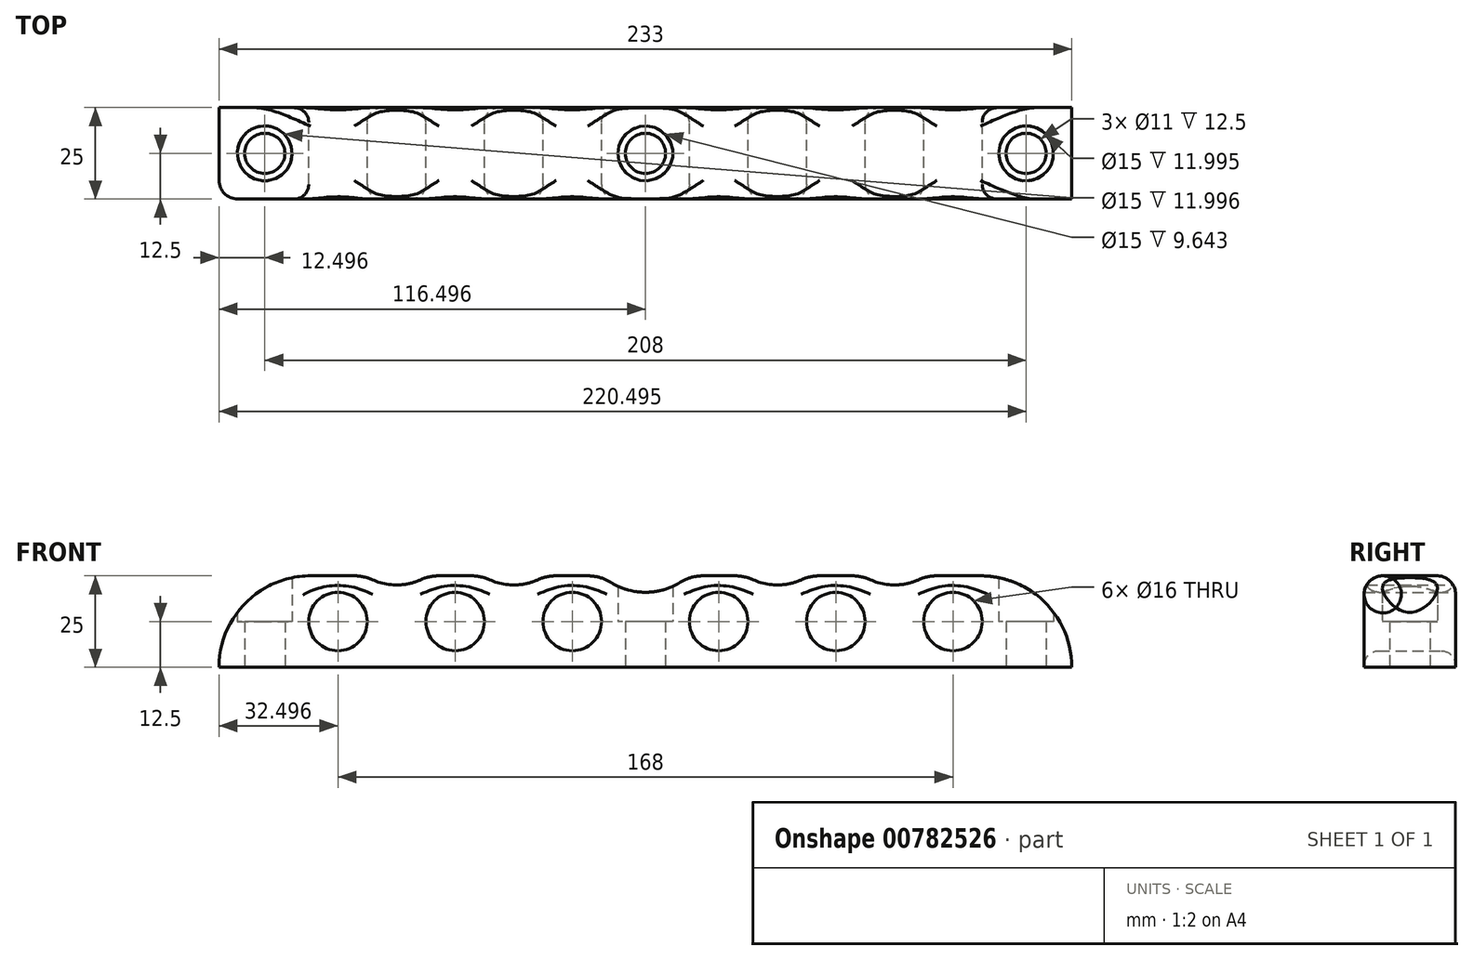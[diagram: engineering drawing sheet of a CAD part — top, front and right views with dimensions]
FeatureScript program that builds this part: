
annotation { "Feature Type Name" : "Feature", "Feature Type Description" : "" }
export const myFeature = defineFeature(function(context is Context, id is Id, definition is map)
    precondition{}
    {
        {
            var Q0;
            Q0=qCreatedBy(makeId("Front.planeOp"),FACE);
            var sketch = newSketch(context, id + "F0", { "sketchPlane" : qUnion([Q0])});
            skLineSegment(sketch, "E0", {"start": v(-90.93, 0) * mm, "end": v(142.07, 0) * mm});
            skArc(sketch, "E1", {"start": v(-90.93, 0) * mm, "mid": v(-77.77, 22.02) * mm, "end": v(-52.14, 20.85) * mm});
            skArc(sketch, "E2", {"start": v(142.07, 0) * mm, "mid": v(127.68, 22.63) * mm, "end": v(101.09, 19.23) * mm});
            skCircle(sketch, "E3", {"center": v(-58.43, 12.5) * mm, "radius": 8 * mm});
            skCircle(sketch, "E4", {"center": v(-26.43, 12.5) * mm, "radius": 8 * mm});
            skCircle(sketch, "E5", {"center": v(5.57, 12.5) * mm, "radius": 8 * mm});
            skCircle(sketch, "E6", {"center": v(45.57, 12.5) * mm, "radius": 8 * mm});
            skCircle(sketch, "E7", {"center": v(77.57, 12.5) * mm, "radius": 8 * mm});
            skCircle(sketch, "E8", {"center": v(109.57, 12.5) * mm, "radius": 8 * mm});
            skLineSegment(sketch, "E9", {"start": v(-65.93, 25) * mm, "end": v(117.07, 25) * mm});
            skCircle(sketch, "E10", {"center": v(-42.43, 38.5) * mm, "radius": 16 * mm});
            skCircle(sketch, "E11", {"center": v(-10.43, 38.5) * mm, "radius": 16 * mm});
            skCircle(sketch, "E12", {"center": v(25.57, 38.5) * mm, "radius": 18 * mm});
            skCircle(sketch, "E13", {"center": v(61.57, 38.5) * mm, "radius": 16 * mm});
            skCircle(sketch, "E14", {"center": v(93.57, 38.5) * mm, "radius": 16 * mm});
            skSolve(sketch);
        }
        {
            var Q0;
            {var subQ6=sQuery(id+"F0.wireOp",EDGE,"E0");Q0=makeQuery(id+"F0.imprint","IMPRINT",FACE,{"disambiguationData":[TD([[makeQuery(id+"F0.imprint","IMPRINT",EDGE,{"derivedFrom":subQ6}),1.0]])]});}
            extrude(context, id + "F1", {"entities" : qUnion([Q0]), "depth" : 25 * mm, "offsetDistance" : 25.4 * mm});
        }
        {
            var Q0;
            Q0=makeQuery(id+"F1.opExtrude","CAP_EDGE",EDGE,{"disambiguationData":[OSD([sQuery(id+"F0.wireOp",EDGE,"E3")])],"isStart":false});
            var Q1;
            Q1=makeQuery(id+"F1.opExtrude","CAP_EDGE",EDGE,{"disambiguationData":[OSD([sQuery(id+"F0.wireOp",EDGE,"E4")])],"isStart":false});
            var Q2;
            Q2=makeQuery(id+"F1.opExtrude","CAP_EDGE",EDGE,{"disambiguationData":[OSD([sQuery(id+"F0.wireOp",EDGE,"E5")])],"isStart":false});
            var Q3;
            Q3=makeQuery(id+"F1.opExtrude","CAP_EDGE",EDGE,{"disambiguationData":[OSD([sQuery(id+"F0.wireOp",EDGE,"E6")])],"isStart":false});
            var Q4;
            Q4=makeQuery(id+"F1.opExtrude","CAP_EDGE",EDGE,{"disambiguationData":[OSD([sQuery(id+"F0.wireOp",EDGE,"E7")])],"isStart":true});
            var Q5;
            Q5=makeQuery(id+"F1.opExtrude","CAP_EDGE",EDGE,{"disambiguationData":[OSD([sQuery(id+"F0.wireOp",EDGE,"E7")])],"isStart":false});
            var Q6;
            Q6=makeQuery(id+"F1.opExtrude","CAP_EDGE",EDGE,{"disambiguationData":[OSD([sQuery(id+"F0.wireOp",EDGE,"E8")])],"isStart":false});
            var Q7;
            Q7=makeQuery(id+"F1.opExtrude","CAP_EDGE",EDGE,{"disambiguationData":[OSD([sQuery(id+"F0.wireOp",EDGE,"E8")])],"isStart":true});
            var Q8;
            Q8=makeQuery(id+"F1.opExtrude","CAP_EDGE",EDGE,{"disambiguationData":[OSD([sQuery(id+"F0.wireOp",EDGE,"E6")])],"isStart":true});
            var Q9;
            Q9=makeQuery(id+"F1.opExtrude","CAP_EDGE",EDGE,{"disambiguationData":[OSD([sQuery(id+"F0.wireOp",EDGE,"E5")])],"isStart":true});
            var Q10;
            Q10=makeQuery(id+"F1.opExtrude","CAP_EDGE",EDGE,{"disambiguationData":[OSD([sQuery(id+"F0.wireOp",EDGE,"E4")])],"isStart":true});
            var Q11;
            Q11=makeQuery(id+"F1.opExtrude","CAP_EDGE",EDGE,{"disambiguationData":[OSD([sQuery(id+"F0.wireOp",EDGE,"E3")])],"isStart":true});
            fillet(context, id + "F2", {"entities" : qUnion([Q0, Q1, Q2, Q3, Q4, Q5, Q6, Q7, Q8, Q9, Q10, Q11]), "radius" : 4 * mm, "tangentPropagation" : true, "allowEdgeOverflow" : false});
        }
        {
            var Q0;
            Q0=qCreatedBy(makeId("Top.planeOp"),FACE);
            var sketch = newSketch(context, id + "F3", { "sketchPlane" : qUnion([Q0])});
            skCircle(sketch, "E15", {"center": v(-78.43, -12.5) * mm, "radius": 7.5 * mm});
            skCircle(sketch, "E16", {"center": v(129.57, -12.5) * mm, "radius": 7.5 * mm});
            skCircle(sketch, "E17", {"center": v(-78.43, -12.5) * mm, "radius": 5.5 * mm});
            skCircle(sketch, "E18", {"center": v(129.57, -12.5) * mm, "radius": 5.5 * mm});
            skCircle(sketch, "E19", {"center": v(25.57, -12.5) * mm, "radius": 7.5 * mm});
            skCircle(sketch, "E20", {"center": v(25.57, -12.5) * mm, "radius": 5.5 * mm});
            skSolve(sketch);
        }
        {
            var Q0;
            Q0=makeQuery(id+"F3.imprint","IMPRINT",FACE,{"disambiguationData":[TD([[makeQuery(id+"F3.imprint","IMPRINT",EDGE,{"derivedFrom":sQuery(id+"F3.wireOp",EDGE,"E17")}),1.0]])]});
            var Q1;
            Q1=makeQuery(id+"F3.imprint","IMPRINT",FACE,{"disambiguationData":[TD([[makeQuery(id+"F3.imprint","IMPRINT",EDGE,{"derivedFrom":sQuery(id+"F3.wireOp",EDGE,"E18")}),1.0]])]});
            extrude(context, id + "F4", {"entities" : qUnion([Q0, Q1]), "operationType" : NewBodyOperationType.REMOVE, "depth" : 25.4 * mm, "offsetDistance" : 25.4 * mm});
        }
        {
            var Q0;
            Q0=makeQuery(id+"F3.imprint","IMPRINT",FACE,{"disambiguationData":[TD([[makeQuery(id+"F3.imprint","IMPRINT",EDGE,{"derivedFrom":sQuery(id+"F3.wireOp",EDGE,"E15")}),1.0]])]});
            var Q1;
            Q1=makeQuery(id+"F3.imprint","IMPRINT",FACE,{"disambiguationData":[TD([[makeQuery(id+"F3.imprint","IMPRINT",EDGE,{"derivedFrom":sQuery(id+"F3.wireOp",EDGE,"E16")}),1.0]])]});
            extrude(context, id + "F5", {"entities" : qUnion([Q0, Q1]), "operationType" : NewBodyOperationType.REMOVE, "depth" : 25.4 * mm, "offsetDistance" : 25.4 * mm});
        }
        {
            var Q0;
            Q0=makeQuery(id+"F3.imprint","IMPRINT",FACE,{"disambiguationData":[TD([[makeQuery(id+"F3.imprint","IMPRINT",EDGE,{"derivedFrom":sQuery(id+"F3.wireOp",EDGE,"E16")}),1.0]])]});
            var Q1;
            Q1=makeQuery(id+"F3.imprint","IMPRINT",FACE,{"disambiguationData":[TD([[makeQuery(id+"F3.imprint","IMPRINT",EDGE,{"derivedFrom":sQuery(id+"F3.wireOp",EDGE,"E15")}),1.0]])]});
            extrude(context, id + "F6", {"entities" : qUnion([Q0, Q1]), "operationType" : NewBodyOperationType.ADD, "depth" : 12.5 * mm, "offsetDistance" : 25.4 * mm});
        }
        {
            var Q0;
            {var subQ0=sQuery(id+"F0.wireOp",EDGE,"E9");Q0=makeQuery(id+"F1.opExtrude","CAP_EDGE",EDGE,{"disambiguationData":[OSD([subQ0]),TDD([makeQuery(id+"F0.imprint","IMPRINT",EDGE,{"disambiguationData":[TD([[makeQuery(id+"F0.imprint","INTERSECT",VERTEX,{"derivedFrom":[sQuery(id+"F0.wireOp",EDGE,"E1"),subQ0]}),-1.0]])],"derivedFrom":subQ0})])],"isStart":false});}
            var Q1;
            {var subQ0=sQuery(id+"F0.wireOp",EDGE,"E9");Q1=makeQuery(id+"F1.opExtrude","CAP_EDGE",EDGE,{"disambiguationData":[OSD([subQ0]),TDD([makeQuery(id+"F0.imprint","IMPRINT",EDGE,{"disambiguationData":[TD([[makeQuery(id+"F0.imprint","INTERSECT",VERTEX,{"disambiguationData":[OD(1.0)],"derivedFrom":[subQ0,sQuery(id+"F0.wireOp",EDGE,"E13")]}),-1.0]])],"derivedFrom":subQ0})])],"isStart":true});}
            fillet(context, id + "F7", {"entities" : qUnion([Q0, Q1]), "radius" : 5.08 * mm, "tangentPropagation" : true, "allowEdgeOverflow" : false});
        }
        {
            var Q0;
            {var subQ0=sQuery(id+"F0.wireOp",EDGE,"E10");var subQ1=sQuery(id+"F0.wireOp",EDGE,"E9");Q0=makeQuery(id+"F1.opExtrude","SWEPT_EDGE",EDGE,{"disambiguationData":[OSD([subQ1,subQ0]),TDD([makeQuery(id+"F0.imprint","INTERSECT",VERTEX,{"disambiguationData":[OD(0.0)],"derivedFrom":[subQ1,subQ0]})])]});}
            var Q1;
            {var subQ0=sQuery(id+"F0.wireOp",EDGE,"E10");var subQ1=sQuery(id+"F0.wireOp",EDGE,"E9");Q1=makeQuery(id+"F1.opExtrude","SWEPT_EDGE",EDGE,{"disambiguationData":[OSD([subQ1,subQ0]),TDD([makeQuery(id+"F0.imprint","INTERSECT",VERTEX,{"disambiguationData":[OD(1.0)],"derivedFrom":[subQ1,subQ0]})])]});}
            var Q2;
            {var subQ0=sQuery(id+"F0.wireOp",EDGE,"E11");var subQ1=sQuery(id+"F0.wireOp",EDGE,"E9");Q2=makeQuery(id+"F1.opExtrude","SWEPT_EDGE",EDGE,{"disambiguationData":[OSD([subQ1,subQ0]),TDD([makeQuery(id+"F0.imprint","INTERSECT",VERTEX,{"disambiguationData":[OD(0.0)],"derivedFrom":[subQ1,subQ0]})])]});}
            var Q3;
            {var subQ0=sQuery(id+"F0.wireOp",EDGE,"E11");var subQ1=sQuery(id+"F0.wireOp",EDGE,"E9");Q3=makeQuery(id+"F1.opExtrude","SWEPT_EDGE",EDGE,{"disambiguationData":[OSD([subQ1,subQ0]),TDD([makeQuery(id+"F0.imprint","INTERSECT",VERTEX,{"disambiguationData":[OD(1.0)],"derivedFrom":[subQ1,subQ0]})])]});}
            var Q4;
            {var subQ0=sQuery(id+"F0.wireOp",EDGE,"E12");var subQ1=sQuery(id+"F0.wireOp",EDGE,"E9");Q4=makeQuery(id+"F1.opExtrude","SWEPT_EDGE",EDGE,{"disambiguationData":[OSD([subQ1,subQ0]),TDD([makeQuery(id+"F0.imprint","INTERSECT",VERTEX,{"disambiguationData":[OD(0.0)],"derivedFrom":[subQ1,subQ0]})])]});}
            var Q5;
            {var subQ0=sQuery(id+"F0.wireOp",EDGE,"E12");var subQ1=sQuery(id+"F0.wireOp",EDGE,"E9");Q5=makeQuery(id+"F1.opExtrude","SWEPT_EDGE",EDGE,{"disambiguationData":[OSD([subQ1,subQ0]),TDD([makeQuery(id+"F0.imprint","INTERSECT",VERTEX,{"disambiguationData":[OD(1.0)],"derivedFrom":[subQ1,subQ0]})])]});}
            var Q6;
            {var subQ0=sQuery(id+"F0.wireOp",EDGE,"E13");var subQ1=sQuery(id+"F0.wireOp",EDGE,"E9");Q6=makeQuery(id+"F1.opExtrude","SWEPT_EDGE",EDGE,{"disambiguationData":[OSD([subQ1,subQ0]),TDD([makeQuery(id+"F0.imprint","INTERSECT",VERTEX,{"disambiguationData":[OD(0.0)],"derivedFrom":[subQ1,subQ0]})])]});}
            var Q7;
            {var subQ0=sQuery(id+"F0.wireOp",EDGE,"E13");var subQ1=sQuery(id+"F0.wireOp",EDGE,"E9");Q7=makeQuery(id+"F1.opExtrude","SWEPT_EDGE",EDGE,{"disambiguationData":[OSD([subQ1,subQ0]),TDD([makeQuery(id+"F0.imprint","INTERSECT",VERTEX,{"disambiguationData":[OD(1.0)],"derivedFrom":[subQ1,subQ0]})])]});}
            var Q8;
            {var subQ0=sQuery(id+"F0.wireOp",EDGE,"E14");var subQ1=sQuery(id+"F0.wireOp",EDGE,"E9");Q8=makeQuery(id+"F1.opExtrude","SWEPT_EDGE",EDGE,{"disambiguationData":[OSD([subQ1,subQ0]),TDD([makeQuery(id+"F0.imprint","INTERSECT",VERTEX,{"disambiguationData":[OD(1.0)],"derivedFrom":[subQ1,subQ0]})])]});}
            var Q9;
            {var subQ0=sQuery(id+"F0.wireOp",EDGE,"E14");var subQ1=sQuery(id+"F0.wireOp",EDGE,"E9");Q9=makeQuery(id+"F1.opExtrude","SWEPT_EDGE",EDGE,{"disambiguationData":[OSD([subQ1,subQ0]),TDD([makeQuery(id+"F0.imprint","INTERSECT",VERTEX,{"disambiguationData":[OD(0.0)],"derivedFrom":[subQ1,subQ0]})])]});}
            fillet(context, id + "F8", {"entities" : qUnion([Q0, Q1, Q2, Q3, Q4, Q5, Q6, Q7, Q8, Q9]), "radius" : 12 * mm, "allowEdgeOverflow" : false});
        }
        {
            var Q0;
            Q0=makeQuery(id+"F3.imprint","IMPRINT",FACE,{"disambiguationData":[TD([[makeQuery(id+"F3.imprint","IMPRINT",EDGE,{"derivedFrom":sQuery(id+"F3.wireOp",EDGE,"E20")}),1.0]])]});
            var Q1;
            Q1=makeQuery(id+"F3.imprint","IMPRINT",FACE,{"disambiguationData":[TD([[makeQuery(id+"F3.imprint","IMPRINT",EDGE,{"derivedFrom":sQuery(id+"F3.wireOp",EDGE,"E19")}),1.0]])]});
            extrude(context, id + "F9", {"entities" : qUnion([Q0, Q1]), "operationType" : NewBodyOperationType.REMOVE, "depth" : 25 * mm, "offsetDistance" : 25 * mm});
        }
        {
            var Q0;
            Q0=makeQuery(id+"F3.imprint","IMPRINT",FACE,{"disambiguationData":[TD([[makeQuery(id+"F3.imprint","IMPRINT",EDGE,{"derivedFrom":sQuery(id+"F3.wireOp",EDGE,"E19")}),1.0]])]});
            extrude(context, id + "F10", {"entities" : qUnion([Q0]), "operationType" : NewBodyOperationType.ADD, "depth" : 12.5 * mm, "offsetDistance" : 25 * mm});
        }
    });
